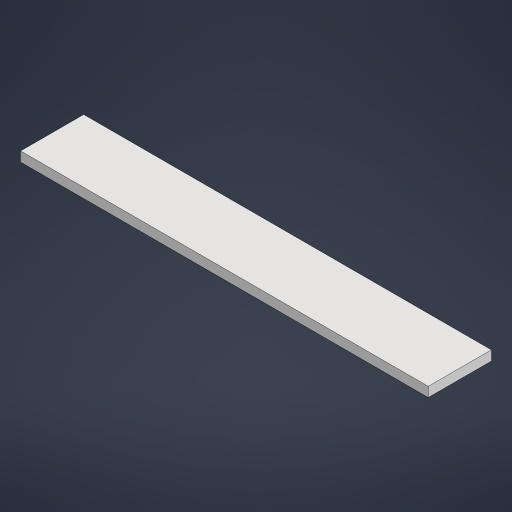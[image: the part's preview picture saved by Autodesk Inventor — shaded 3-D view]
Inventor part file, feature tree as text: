
AUTODESK INVENTOR PART (.ipt)
format: ipt  version: 2023.2 (Build 272271000, 271)  size: 160,768 bytes
history: native  units: in
note: dims shown in document units (in); Inventor stores cm internally (conversion verified against a paired STEP export)
features: extrude x1, sketch x1
ambient origin geometry x8: Origin, YZ Plane, XZ Plane, XY Plane, X Axis, Y Axis, Z Axis, Center Point
bodies: Solid1 (feature_tree)
feature tree (2):
  extrude  "Extrusion1"  Depth=13.0in
  sketch  "Sketch2"  dims[d3=84.0in d4=13.0in d5=2.0in d6=0.0in]
